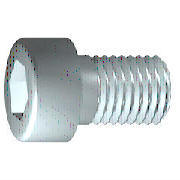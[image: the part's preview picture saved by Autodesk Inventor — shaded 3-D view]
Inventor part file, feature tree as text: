
AUTODESK INVENTOR PART (.ipt)
format: ipt  version: 2020 (Build 240168000, 168)  size: 193,024 bytes
history: native  units: mm (DEFAULTED — no unit token found)
features: sketch x2, extrude x1, plane x1, fillet x1
ambient origin geometry x7: Origin, YZ Plane, XY Plane, X Axis, Y Axis, Z Axis, Center Point
bodies: Solid1 (feature_tree), Body (feature_tree)
feature tree (5):
  extrude  "Slot"  Depth=3.5mm
  plane  "Work Plane1"
  fillet  "Fillet2"  Radius=3.5mm
  sketch  "Sketch1"  dims[d1=17.6mm d2=0.49086mm d3=3.5mm]
  sketch  "Sketch2"  dims[d4=2.7mm d5=60.0deg d6=5.0mm d7=5.0mm d8=3.464102mm d9=8.5mm d10=90.0deg d11=10.0mm d12=0.0mm d13=17.6mm d14=0.0mm d15=0.49076mm d16=0.49076mm d17=0.5mm d19=0.0mm d26=20.0mm d27=45.0deg d28=0.0mm d29=0.0mm d30=0.1mm]
